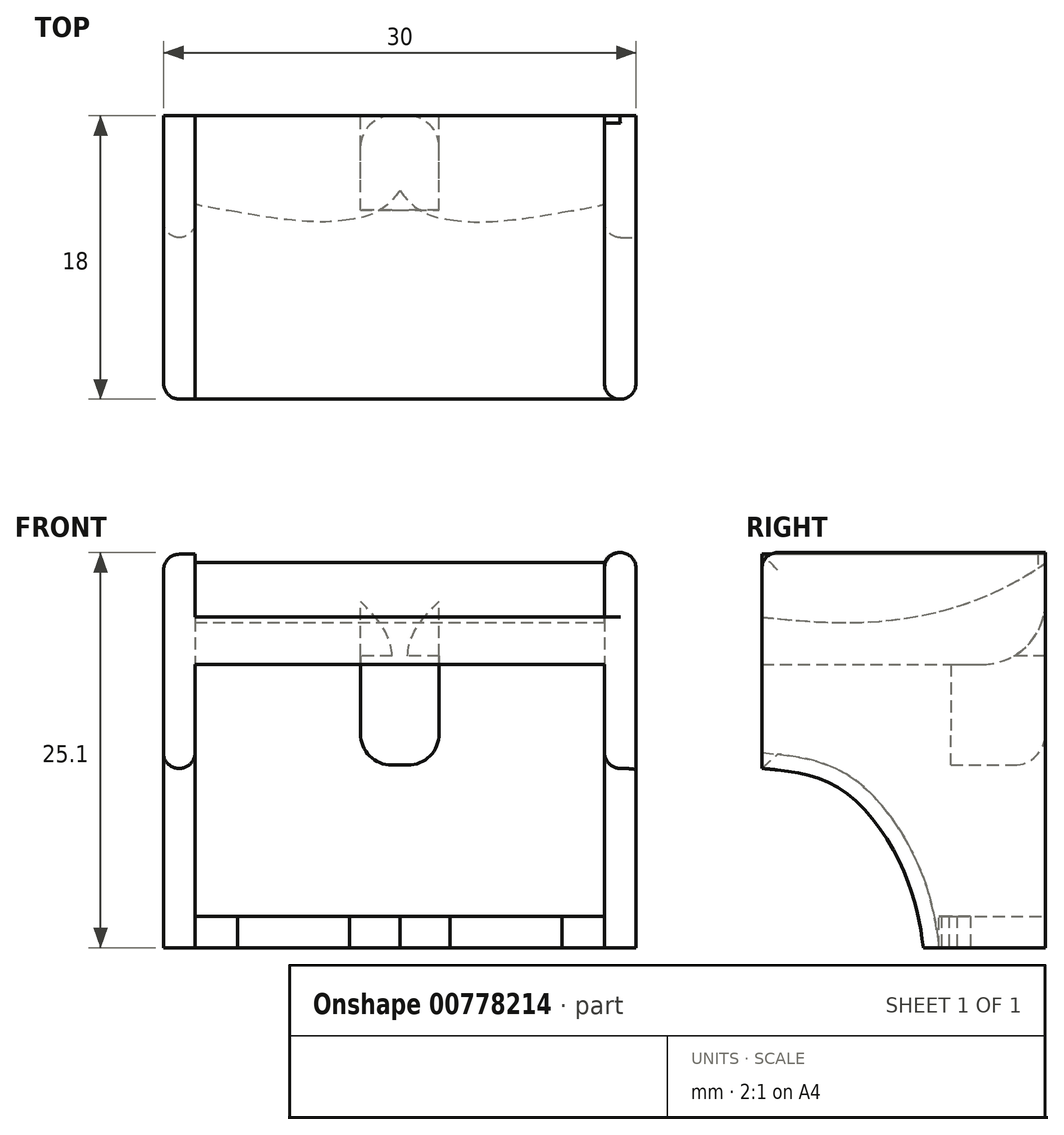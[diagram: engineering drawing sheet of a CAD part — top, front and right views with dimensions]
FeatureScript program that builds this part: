
annotation { "Feature Type Name" : "Feature", "Feature Type Description" : "" }
export const myFeature = defineFeature(function(context is Context, id is Id, definition is map)
    precondition{}
    {
        {
            var Q0;
            Q0=qCreatedBy(makeId("Front.planeOp"),FACE);
            var sketch = newSketch(context, id + "F0", { "sketchPlane" : qUnion([Q0])});
            skLineSegment(sketch, "E0.bottom", {"start": v(0, 0) * mm, "end": v(30, 0) * mm});
            skLineSegment(sketch, "E0.top", {"start": v(0, 20) * mm, "end": v(30, 20) * mm});
            skLineSegment(sketch, "E0.left", {"start": v(0, 0) * mm, "end": v(0, 20) * mm});
            skLineSegment(sketch, "E0.right", {"start": v(30, 0) * mm, "end": v(30, 20) * mm});
            skLineSegment(sketch, "E1.0", {"start": v(2, 18) * mm, "end": v(12.5, 18) * mm});
            skLineSegment(sketch, "E1.1", {"start": v(2, 2) * mm, "end": v(2, 18) * mm});
            skLineSegment(sketch, "E1.2", {"start": v(2, 2) * mm, "end": v(28, 2) * mm});
            skLineSegment(sketch, "E1.3", {"start": v(28, 2) * mm, "end": v(28, 18) * mm});
            skLineSegment(sketch, "E2", {"start": v(15, 11.6) * mm, "end": v(15, 0) * mm, "construction": true});
            skLineSegment(sketch, "E3.bottom", {"start": v(15, 20) * mm, "end": v(17.5, 20) * mm});
            skLineSegment(sketch, "E3.top", {"start": v(15, 11.6) * mm, "end": v(17.5, 11.6) * mm});
            skLineSegment(sketch, "E3.right", {"start": v(17.5, 18) * mm, "end": v(17.5, 11.6) * mm});
            skLineSegment(sketch, "E4.MirrorCS", {"start": v(15, 11.6) * mm, "end": v(12.5, 11.6) * mm});
            skLineSegment(sketch, "E5.MirrorCS", {"start": v(12.5, 18) * mm, "end": v(12.5, 11.6) * mm});
            skLineSegment(sketch, "E6.trimOffspring", {"start": v(17.5, 18) * mm, "end": v(28, 18) * mm});
            skLineSegment(sketch, "E7", {"start": v(12.5, 18) * mm, "end": v(17.5, 18) * mm});
            skPoint(sketch, "E8.orphan", {"position": v(12.5, 20) * mm});
            skSolve(sketch);
        }
        {
            var Q0;
            Q0=makeQuery(id+"F0.imprint","IMPRINT",FACE,{"disambiguationData":[TD([[makeQuery(id+"F0.imprint","IMPRINT",EDGE,{"derivedFrom":sQuery(id+"F0.wireOp",EDGE,"E0.bottom")}),1.0]])]});
            var Q1;
            Q1=makeQuery(id+"F0.imprint","IMPRINT",FACE,{"disambiguationData":[TD([[makeQuery(id+"F0.imprint","IMPRINT",EDGE,{"derivedFrom":sQuery(id+"F0.wireOp",EDGE,"E3.top")}),1.0]])]});
            extrude(context, id + "F1", {"entities" : qUnion([Q0, Q1]), "depth" : 18 * mm, "offsetDistance" : 25 * mm});
        }
        {
            var Q0;
            Q0=makeQuery(id+"F1.opExtrude","SWEPT_FACE",FACE,{"disambiguationData":[OSD([sQuery(id+"F0.wireOp",EDGE,"E0.bottom")])]});
            var sketch = newSketch(context, id + "F2", { "sketchPlane" : qUnion([Q0])});
            skLineSegment(sketch, "E9", {"start": v(2, 18) * mm, "end": v(2, 0) * mm});
            skLineSegment(sketch, "E10", {"start": v(28, 18) * mm, "end": v(28, 0) * mm});
            skLineSegment(sketch, "E11", {"start": v(15, 18) * mm, "end": v(15, 0) * mm, "construction": true});
            skFitSpline(sketch, "E12", {"points": [v(15, 4.76) * mm, v(11.82, 6.58) * mm, v(2, 5.61) * mm, v(2, 5.6) * mm], "startDerivative": vector(-5.14, 6.62) * mm, "endDerivative": vector(0.38, -0.52) * mm});
            skFitSpline(sketch, "E13.MirrorCS", {"points": [v(15, 4.76) * mm, v(18.18, 6.58) * mm, v(28, 5.61) * mm, v(28, 5.6) * mm], "startDerivative": vector(5.14, 6.62) * mm, "endDerivative": vector(-0.38, -0.52) * mm});
            skFitSpline(sketch, "E14", {"points": [v(15, 4.76) * mm, v(11.82, 6.58) * mm, v(2, 5.61) * mm], "startDerivative": vector(-7, 6.03) * mm, "endDerivative": vector(-18.1, -3.55) * mm});
            skFitSpline(sketch, "E15.MirrorCS", {"points": [v(15, 4.76) * mm, v(18.18, 6.58) * mm, v(28, 5.61) * mm], "startDerivative": vector(7, 6.03) * mm, "endDerivative": vector(18.1, -3.55) * mm});
            skSolve(sketch);
        }
        {
            var Q0;
            {var subQ3=sQuery(id+"F2.wireOp",EDGE,"E9");var subQ5=makeQuery(id+"F1.opExtrude","CAP_EDGE",EDGE,{"disambiguationData":[OSD([sQuery(id+"F0.wireOp",EDGE,"E0.bottom")])],"isStart":false});var subQ6=makeQuery(id+"F2.imprint","INTERSECT",VERTEX,{"derivedFrom":[subQ5,subQ3]});Q0=makeQuery(id+"F2.imprint","IMPRINT",FACE,{"disambiguationData":[TD([[makeQuery(id+"F2.imprint","IMPRINT",EDGE,{"disambiguationData":[TD([[subQ6,-1.0]])],"derivedFrom":subQ3}),1.0]])]});}
            extrude(context, id + "F3", {"entities" : qUnion([Q0]), "operationType" : NewBodyOperationType.REMOVE, "oppositeDirection" : true, "depth" : 2 * mm, "offsetDistance" : 25 * mm});
        }
        {
            var Q0;
            Q0=makeQuery(id+"F1.opExtrude","SWEPT_FACE",FACE,{"disambiguationData":[OSD([sQuery(id+"F0.wireOp",EDGE,"E0.right")])]});
            var sketch = newSketch(context, id + "F4", { "sketchPlane" : qUnion([Q0])});
            skPoint(sketch, "E16.1.internal.snap0", {"position": v(-18, 10) * mm});
            skFitSpline(sketch, "E16", {"points": [v(-18, 11.4) * mm, v(-12.88, 10) * mm, v(-8.83, 4.5) * mm, v(-7.74, 0) * mm], "startDerivative": vector(16.41, -1.59) * mm, "endDerivative": vector(2.12, -14.06) * mm});
            skSolve(sketch);
        }
        {
            var Q0;
            {var subQ0=sQuery(id+"F4.wireOp",EDGE,"E16");Q0=makeQuery(id+"F4.imprint","IMPRINT",FACE,{"disambiguationData":[TD([[makeQuery(id+"F4.imprint","IMPRINT",EDGE,{"derivedFrom":subQ0}),-1.0]])]});}
            extrude(context, id + "F5", {"entities" : qUnion([Q0]), "operationType" : NewBodyOperationType.REMOVE, "endBound" : BoundingType.THROUGH_ALL, "oppositeDirection" : true, "depth" : 25 * mm, "offsetDistance" : 25 * mm});
        }
        {
            var Q0;
            Q0=makeQuery(id+"F1.opExtrude","SWEPT_FACE",FACE,{"disambiguationData":[OSD([sQuery(id+"F0.wireOp",EDGE,"E0.top"),sQuery(id+"F0.wireOp",EDGE,"E3.bottom")])]});
            extrude(context, id + "F6", {"entities" : qUnion([Q0]), "operationType" : NewBodyOperationType.ADD, "depth" : 5 * mm, "offsetDistance" : 25 * mm});
        }
        {
            var Q0;
            {var subQ0=sQuery(id+"F0.wireOp",EDGE,"E0.right");Q0=makeQuery(id+"F6.boolean.opBoolean","MERGE",FACE,{"derivedFrom":[makeQuery(id+"F1.opExtrude","SWEPT_FACE",FACE,{"disambiguationData":[OSD([subQ0])]}),makeQuery(id+"F6.opExtrude","SWEPT_FACE",FACE,{"disambiguationData":[OSD([sQuery(id+"F0.wireOp",EDGE,"E0.top"),subQ0])]})]});}
            var sketch = newSketch(context, id + "F7", { "sketchPlane" : qUnion([Q0])});
            skLineSegment(sketch, "E17", {"start": v(-18, 20.2) * mm, "end": v(0, 20.2) * mm, "construction": true});
            skFitSpline(sketch, "E18", {"points": [v(-18, 21) * mm, v(-11.59, 20.68) * mm, v(-3.7, 22.37) * mm, v(0, 24.47) * mm, v(0, 24.5) * mm], "startDerivative": vector(18.68, -1.89) * mm, "endDerivative": vector(-0.52, 1.05) * mm});
            skSolve(sketch);
        }
        {
            var Q0;
            {var subQ0=sQuery(id+"F0.wireOp",EDGE,"E3.bottom");var subQ1=sQuery(id+"F0.wireOp",EDGE,"E0.top");Q0=makeQuery(id+"F6.boolean.opBoolean","MERGE",FACE,{"derivedFrom":[makeQuery(id+"F1.opExtrude","CAP_FACE",FACE,{"disambiguationData":[OSD([sQuery(id+"F0.wireOp",EDGE,"E0.bottom"),subQ1,sQuery(id+"F0.wireOp",EDGE,"E0.left"),sQuery(id+"F0.wireOp",EDGE,"E0.right"),sQuery(id+"F0.wireOp",EDGE,"E1.0"),sQuery(id+"F0.wireOp",EDGE,"E1.1"),sQuery(id+"F0.wireOp",EDGE,"E1.2"),sQuery(id+"F0.wireOp",EDGE,"E1.3"),subQ0,sQuery(id+"F0.wireOp",EDGE,"E3.top"),sQuery(id+"F0.wireOp",EDGE,"E3.right"),sQuery(id+"F0.wireOp",EDGE,"E4.MirrorCS"),sQuery(id+"F0.wireOp",EDGE,"E5.MirrorCS"),sQuery(id+"F0.wireOp",EDGE,"E6.trimOffspring")])],"isStart":false}),makeQuery(id+"F6.opExtrude","SWEPT_FACE",FACE,{"disambiguationData":[OSD([subQ1,subQ0]),TDD([makeQuery(id+"F1.opExtrude","CAP_EDGE",EDGE,{"disambiguationData":[OSD([subQ1,subQ0])],"isStart":false})])]})]});}
            var sketch = newSketch(context, id + "F8", { "sketchPlane" : qUnion([Q0])});
            skLineSegment(sketch, "E19", {"start": v(2, 18) * mm, "end": v(2, 25) * mm, "construction": true});
            skSolve(sketch);
        }
        {
            var Q0;
            {var subQ1=sQuery(id+"F0.wireOp",EDGE,"E0.right");var subQ2=sQuery(id+"F0.wireOp",EDGE,"E0.top");var subQ6=makeQuery(id+"F6.opExtrude","CAP_EDGE",EDGE,{"disambiguationData":[OSD([subQ2,subQ1])],"isStart":false});Q0=makeQuery(id+"F7.imprint","IMPRINT",FACE,{"disambiguationData":[TD([[makeQuery(id+"F7.imprint","IMPRINT",EDGE,{"derivedFrom":subQ6}),-1.0]])]});}
            extrude(context, id + "F9", {"entities" : qUnion([Q0]), "operationType" : NewBodyOperationType.REMOVE, "oppositeDirection" : true, "depth" : 28 * mm, "offsetDistance" : 25 * mm});
        }
        {
            var Q0;
            {var subQ0=sQuery(id+"F0.wireOp",EDGE,"E0.right");Q0=makeQuery(id+"F6.boolean.opBoolean","MERGE",FACE,{"derivedFrom":[makeQuery(id+"F1.opExtrude","SWEPT_FACE",FACE,{"disambiguationData":[OSD([subQ0])]}),makeQuery(id+"F6.opExtrude","SWEPT_FACE",FACE,{"disambiguationData":[OSD([sQuery(id+"F0.wireOp",EDGE,"E0.top"),subQ0])]})]});}
            var sketch = newSketch(context, id + "F10", { "sketchPlane" : qUnion([Q0])});
            skLineSegment(sketch, "E20", {"start": v(-18, 20.1) * mm, "end": v(0, 20.1) * mm, "construction": true});
            skFitSpline(sketch, "E21", {"points": [v(-18, 20.91) * mm, v(-11.59, 20.59) * mm, v(-3.7, 22.28) * mm, v(0, 24.38) * mm, v(0, 24.42) * mm], "startDerivative": vector(18.68, -1.89) * mm, "endDerivative": vector(-0.52, 1.05) * mm});
            skLineSegment(sketch, "E22", {"start": v(-18, 20.1) * mm, "end": v(0, 20.1) * mm});
            skSolve(sketch);
        }
        {
            var Q0;
            {var subQ7=sQuery(id+"F10.wireOp",EDGE,"E22");Q0=makeQuery(id+"F10.imprint","IMPRINT",FACE,{"disambiguationData":[TD([[makeQuery(id+"F10.imprint","IMPRINT",EDGE,{"derivedFrom":subQ7}),1.0]])]});}
            extrude(context, id + "F11", {"entities" : qUnion([Q0]), "operationType" : NewBodyOperationType.REMOVE, "oppositeDirection" : true, "depth" : 2 * mm, "offsetDistance" : 25 * mm});
        }
        {
            var Q0;
            Q0=makeQuery(id+"F11.boolean.opBoolean","COPY",FACE,{"derivedFrom":makeQuery(id+"F11.opExtrude","SWEPT_FACE",FACE,{"disambiguationData":[OSD([sQuery(id+"F10.wireOp",EDGE,"E22")])]})});
            extrude(context, id + "F12", {"entities" : qUnion([Q0]), "operationType" : NewBodyOperationType.ADD, "depth" : 5 * mm, "offsetDistance" : 25 * mm});
        }
        {
            var Q0;
            Q0=makeQuery(id+"F1.opExtrude","CAP_EDGE",EDGE,{"disambiguationData":[OSD([sQuery(id+"F0.wireOp",EDGE,"E6.trimOffspring")])],"isStart":true});
            var Q1;
            Q1=makeQuery(id+"F1.opExtrude","CAP_EDGE",EDGE,{"disambiguationData":[OSD([sQuery(id+"F0.wireOp",EDGE,"E1.0")])],"isStart":true});
            fillet(context, id + "F13", {"entities" : qUnion([Q0, Q1]), "radius" : 4 * mm, "tangentPropagation" : true, "allowEdgeOverflow" : false});
        }
        {
            var Q0;
            Q0=makeQuery(id+"F1.opExtrude","CAP_EDGE",EDGE,{"disambiguationData":[OSD([sQuery(id+"F0.wireOp",EDGE,"E3.right")])],"isStart":true});
            var Q1;
            Q1=makeQuery(id+"F1.opExtrude","CAP_EDGE",EDGE,{"disambiguationData":[OSD([sQuery(id+"F0.wireOp",EDGE,"E5.MirrorCS")])],"isStart":true});
            fillet(context, id + "F14", {"entities" : qUnion([Q0, Q1]), "radius" : 2 * mm, "tangentPropagation" : true, "allowEdgeOverflow" : false});
        }
        {
            var Q0;
            {var subQ11=sQuery(id+"F0.wireOp",EDGE,"E1.0");Q0=makeQuery(id+"F8.imprint","IMPRINT",FACE,{"disambiguationData":[TD([[makeQuery(id+"F8.imprint","IMPRINT",EDGE,{"derivedFrom":makeQuery(id+"F1.opExtrude","CAP_EDGE",EDGE,{"disambiguationData":[OSD([subQ11])],"isStart":false})}),1.0]])]});}
            var sketch = newSketch(context, id + "F15", { "sketchPlane" : qUnion([Q0])});
            skLineSegment(sketch, "E23", {"start": v(17.5, 18) * mm, "end": v(12.5, 18) * mm});
            skSolve(sketch);
        }
        {
            var Q0;
            Q0=makeQuery(id+"F1.opExtrude","SWEPT_FACE",FACE,{"disambiguationData":[OSD([sQuery(id+"F0.wireOp",EDGE,"E3.top"),sQuery(id+"F0.wireOp",EDGE,"E4.MirrorCS")])]});
            var sketch = newSketch(context, id + "F16", { "sketchPlane" : qUnion([Q0])});
            skLineSegment(sketch, "E24", {"start": v(12.5, 12) * mm, "end": v(17.5, 12) * mm});
            skSolve(sketch);
        }
        {
            var Q0;
            {var subQ0=sQuery(id+"F16.wireOp",EDGE,"E24");Q0=makeQuery(id+"F16.imprint","IMPRINT",FACE,{"disambiguationData":[TD([[makeQuery(id+"F16.imprint","IMPRINT",EDGE,{"derivedFrom":subQ0}),1.0]])]});}
            extrude(context, id + "F17", {"entities" : qUnion([Q0]), "operationType" : NewBodyOperationType.REMOVE, "oppositeDirection" : true, "depth" : 6.4 * mm, "offsetDistance" : 25 * mm});
        }
        {
            var Q0;
            {var subQ0=sQuery(id+"F7.wireOp",EDGE,"E18");var subQ1=sQuery(id+"F0.wireOp",EDGE,"E0.right");var subQ2=sQuery(id+"F0.wireOp",EDGE,"E0.top");Q0=makeQuery(id+"F9.boolean.opBoolean","COPY",EDGE,{"derivedFrom":makeQuery(id+"F9.opExtrude","SWEPT_EDGE",EDGE,{"disambiguationData":[OSD([subQ2,subQ1,subQ0]),TDD([makeQuery(id+"F7.imprint","INTERSECT",VERTEX,{"derivedFrom":[makeQuery(id+"F6.boolean.opBoolean","MERGE",EDGE,{"derivedFrom":[makeQuery(id+"F1.opExtrude","CAP_EDGE",EDGE,{"disambiguationData":[OSD([subQ1])],"isStart":false}),makeQuery(id+"F6.opExtrude","SWEPT_EDGE",EDGE,{"disambiguationData":[OSD([subQ2,subQ1]),TDD([makeQuery(id+"F1.opExtrude","CAP_VERTEX",VERTEX,{"disambiguationData":[OSD([subQ2,subQ1])],"isStart":false})])]})]}),subQ0]})])]})});}
            var Q1;
            Q1=makeQuery(id+"F17.boolean.opBoolean","MERGE",EDGE,{"derivedFrom":[makeQuery(id+"F1.opExtrude","CAP_EDGE",EDGE,{"disambiguationData":[OSD([sQuery(id+"F0.wireOp",EDGE,"E1.0")])],"isStart":false}),makeQuery(id+"F1.opExtrude","CAP_EDGE",EDGE,{"disambiguationData":[OSD([sQuery(id+"F0.wireOp",EDGE,"E6.trimOffspring")])],"isStart":false}),makeQuery(id+"F17.opExtrude","CAP_EDGE",EDGE,{"disambiguationData":[OSD([sQuery(id+"F0.wireOp",EDGE,"E3.top"),sQuery(id+"F0.wireOp",EDGE,"E4.MirrorCS")])],"isStart":false})]});
            var Q2;
            Q2=makeQuery(id+"F3.boolean.opBoolean","MERGE",EDGE,{"derivedFrom":[makeQuery(id+"F1.opExtrude","CAP_EDGE",EDGE,{"disambiguationData":[OSD([sQuery(id+"F0.wireOp",EDGE,"E1.3")])],"isStart":false}),makeQuery(id+"F3.opExtrude","SWEPT_EDGE",EDGE,{"disambiguationData":[OSD([sQuery(id+"F0.wireOp",EDGE,"E0.bottom"),sQuery(id+"F2.wireOp",EDGE,"E10")])]})]});
            var Q3;
            {var subQ0=sQuery(id+"F10.wireOp",EDGE,"E22");var subQ1=sQuery(id+"F0.wireOp",EDGE,"E0.right");var subQ2=sQuery(id+"F0.wireOp",EDGE,"E0.top");var subQ3=makeQuery(id+"F6.boolean.opBoolean","MERGE",EDGE,{"derivedFrom":[makeQuery(id+"F1.opExtrude","CAP_EDGE",EDGE,{"disambiguationData":[OSD([subQ1])],"isStart":false}),makeQuery(id+"F6.opExtrude","SWEPT_EDGE",EDGE,{"disambiguationData":[OSD([subQ2,subQ1]),TDD([makeQuery(id+"F1.opExtrude","CAP_VERTEX",VERTEX,{"disambiguationData":[OSD([subQ2,subQ1])],"isStart":false})])]})]});Q3=makeQuery(id+"F12.boolean.opBoolean","MERGE",EDGE,{"derivedFrom":[makeQuery(id+"F11.boolean.opBoolean","SPLIT",EDGE,{"disambiguationData":[TD([makeQuery(id+"F11.opExtrude","SWEPT_FACE",FACE,{"disambiguationData":[OSD([subQ0])]})])],"derivedFrom":subQ3}),makeQuery(id+"F11.boolean.opBoolean","SPLIT",EDGE,{"disambiguationData":[TD([makeQuery(id+"F9.boolean.opBoolean","COPY",FACE,{"derivedFrom":makeQuery(id+"F9.opExtrude","SWEPT_FACE",FACE,{"disambiguationData":[OSD([sQuery(id+"F7.wireOp",EDGE,"E18")])]})})])],"derivedFrom":subQ3}),makeQuery(id+"F12.opExtrude","SWEPT_EDGE",EDGE,{"disambiguationData":[OSD([subQ2,subQ1,subQ0]),TDD([makeQuery(id+"F11.boolean.opBoolean","COPY",VERTEX,{"derivedFrom":makeQuery(id+"F11.opExtrude","CAP_VERTEX",VERTEX,{"disambiguationData":[OSD([subQ2,subQ1,subQ0]),TDD([makeQuery(id+"F10.imprint","INTERSECT",VERTEX,{"derivedFrom":[subQ3,subQ0]})])],"isStart":true})})])]})]});}
            var Q4;
            {var subQ0=sQuery(id+"F10.wireOp",EDGE,"E22");var subQ1=sQuery(id+"F0.wireOp",EDGE,"E0.right");var subQ2=sQuery(id+"F0.wireOp",EDGE,"E0.top");Q4=makeQuery(id+"F12.opExtrude","SWEPT_EDGE",EDGE,{"disambiguationData":[OSD([subQ2,subQ1,subQ0]),TDD([makeQuery(id+"F11.boolean.opBoolean","COPY",VERTEX,{"derivedFrom":makeQuery(id+"F11.opExtrude","CAP_VERTEX",VERTEX,{"disambiguationData":[OSD([subQ2,subQ1,subQ0]),TDD([makeQuery(id+"F10.imprint","INTERSECT",VERTEX,{"derivedFrom":[makeQuery(id+"F6.boolean.opBoolean","MERGE",EDGE,{"derivedFrom":[makeQuery(id+"F1.opExtrude","CAP_EDGE",EDGE,{"disambiguationData":[OSD([subQ1])],"isStart":false}),makeQuery(id+"F6.opExtrude","SWEPT_EDGE",EDGE,{"disambiguationData":[OSD([subQ2,subQ1]),TDD([makeQuery(id+"F1.opExtrude","CAP_VERTEX",VERTEX,{"disambiguationData":[OSD([subQ2,subQ1])],"isStart":false})])]})]}),subQ0]})])],"isStart":false})})])]});}
            var Q5;
            {var subQ0=sQuery(id+"F0.wireOp",EDGE,"E0.left");var subQ1=sQuery(id+"F0.wireOp",EDGE,"E0.top");Q5=makeQuery(id+"F6.boolean.opBoolean","MERGE",EDGE,{"derivedFrom":[makeQuery(id+"F1.opExtrude","CAP_EDGE",EDGE,{"disambiguationData":[OSD([subQ0])],"isStart":false}),makeQuery(id+"F6.opExtrude","SWEPT_EDGE",EDGE,{"disambiguationData":[OSD([subQ1,subQ0]),TDD([makeQuery(id+"F1.opExtrude","CAP_VERTEX",VERTEX,{"disambiguationData":[OSD([subQ1,subQ0])],"isStart":false})])]})]});}
            var Q6;
            Q6=makeQuery(id+"F3.boolean.opBoolean","MERGE",EDGE,{"derivedFrom":[makeQuery(id+"F1.opExtrude","CAP_EDGE",EDGE,{"disambiguationData":[OSD([sQuery(id+"F0.wireOp",EDGE,"E1.1")])],"isStart":false}),makeQuery(id+"F3.opExtrude","SWEPT_EDGE",EDGE,{"disambiguationData":[OSD([sQuery(id+"F0.wireOp",EDGE,"E0.bottom"),sQuery(id+"F2.wireOp",EDGE,"E9")])]})]});
            var Q7;
            Q7=makeQuery(id+"F5.boolean.opBoolean","INTERSECT",EDGE,{"derivedFrom":[makeQuery(id+"F3.boolean.opBoolean","MERGE",FACE,{"derivedFrom":[makeQuery(id+"F1.opExtrude","SWEPT_FACE",FACE,{"disambiguationData":[OSD([sQuery(id+"F0.wireOp",EDGE,"E1.1")])]}),makeQuery(id+"F3.opExtrude","SWEPT_FACE",FACE,{"disambiguationData":[OSD([sQuery(id+"F2.wireOp",EDGE,"E9")])]})]}),makeQuery(id+"F5.opExtrude","SWEPT_FACE",FACE,{"disambiguationData":[OSD([sQuery(id+"F4.wireOp",EDGE,"E16")])]})]});
            var Q8;
            Q8=makeQuery(id+"F5.boolean.opBoolean","INTERSECT",EDGE,{"derivedFrom":[makeQuery(id+"F1.opExtrude","SWEPT_FACE",FACE,{"disambiguationData":[OSD([sQuery(id+"F0.wireOp",EDGE,"E0.left")])]}),makeQuery(id+"F5.opExtrude","SWEPT_FACE",FACE,{"disambiguationData":[OSD([sQuery(id+"F4.wireOp",EDGE,"E16")])]})]});
            var Q9;
            Q9=makeQuery(id+"F5.boolean.opBoolean","INTERSECT",EDGE,{"derivedFrom":[makeQuery(id+"F3.boolean.opBoolean","MERGE",FACE,{"derivedFrom":[makeQuery(id+"F1.opExtrude","SWEPT_FACE",FACE,{"disambiguationData":[OSD([sQuery(id+"F0.wireOp",EDGE,"E1.3")])]}),makeQuery(id+"F3.opExtrude","SWEPT_FACE",FACE,{"disambiguationData":[OSD([sQuery(id+"F2.wireOp",EDGE,"E10")])]})]}),makeQuery(id+"F5.opExtrude","SWEPT_FACE",FACE,{"disambiguationData":[OSD([sQuery(id+"F4.wireOp",EDGE,"E16")])]})]});
            var Q10;
            Q10=makeQuery(id+"F5.boolean.opBoolean","COPY",EDGE,{"derivedFrom":makeQuery(id+"F5.opExtrude","CAP_EDGE",EDGE,{"disambiguationData":[OSD([sQuery(id+"F4.wireOp",EDGE,"E16")])],"isStart":true})});
            var Q11;
            Q11=makeQuery(id+"F3.boolean.opBoolean","COPY",EDGE,{"derivedFrom":makeQuery(id+"F3.opExtrude","CAP_EDGE",EDGE,{"disambiguationData":[OSD([sQuery(id+"F2.wireOp",EDGE,"E15.MirrorCS")])],"isStart":false})});
            var Q12;
            Q12=makeQuery(id+"F3.boolean.opBoolean","COPY",EDGE,{"derivedFrom":makeQuery(id+"F3.opExtrude","CAP_EDGE",EDGE,{"disambiguationData":[OSD([sQuery(id+"F2.wireOp",EDGE,"E15.MirrorCS")])],"isStart":true})});
            var Q13;
            Q13=makeQuery(id+"F3.boolean.opBoolean","COPY",EDGE,{"derivedFrom":makeQuery(id+"F3.opExtrude","CAP_EDGE",EDGE,{"disambiguationData":[OSD([sQuery(id+"F2.wireOp",EDGE,"E14")])],"isStart":false})});
            var Q14;
            Q14=makeQuery(id+"F3.boolean.opBoolean","COPY",EDGE,{"derivedFrom":makeQuery(id+"F3.opExtrude","CAP_EDGE",EDGE,{"disambiguationData":[OSD([sQuery(id+"F2.wireOp",EDGE,"E14")])],"isStart":true})});
            var Q15;
            {var subQ0=sQuery(id+"F10.wireOp",EDGE,"E22");Q15=makeQuery(id+"F12.opExtrude","CAP_EDGE",EDGE,{"disambiguationData":[OSD([subQ0]),TDD([makeQuery(id+"F11.boolean.opBoolean","COPY",EDGE,{"derivedFrom":makeQuery(id+"F11.opExtrude","CAP_EDGE",EDGE,{"disambiguationData":[OSD([subQ0])],"isStart":false})})])],"isStart":false});}
            var Q16;
            {var subQ0=sQuery(id+"F10.wireOp",EDGE,"E22");Q16=makeQuery(id+"F12.opExtrude","CAP_EDGE",EDGE,{"disambiguationData":[OSD([subQ0]),TDD([makeQuery(id+"F11.boolean.opBoolean","COPY",EDGE,{"derivedFrom":makeQuery(id+"F11.opExtrude","CAP_EDGE",EDGE,{"disambiguationData":[OSD([subQ0])],"isStart":true})})])],"isStart":false});}
            var Q17;
            {var subQ0=sQuery(id+"F0.wireOp",EDGE,"E0.right");var subQ1=sQuery(id+"F0.wireOp",EDGE,"E0.top");Q17=makeQuery(id+"F9.boolean.opBoolean","COPY",EDGE,{"derivedFrom":makeQuery(id+"F9.opExtrude","CAP_EDGE",EDGE,{"disambiguationData":[OSD([subQ1,subQ0]),TDD([makeQuery(id+"F7.imprint","IMPRINT",EDGE,{"derivedFrom":makeQuery(id+"F6.opExtrude","CAP_EDGE",EDGE,{"disambiguationData":[OSD([subQ1,subQ0])],"isStart":false})})])],"isStart":false})});}
            var Q18;
            Q18=makeQuery(id+"F6.opExtrude","CAP_EDGE",EDGE,{"disambiguationData":[OSD([sQuery(id+"F0.wireOp",EDGE,"E0.top"),sQuery(id+"F0.wireOp",EDGE,"E0.left")])],"isStart":false});
            fillet(context, id + "F18", {"entities" : qUnion([Q0, Q1, Q2, Q3, Q4, Q5, Q6, Q7, Q8, Q9, Q10, Q11, Q12, Q13, Q14, Q15, Q16, Q17, Q18]), "radius" : 1 * mm, "tangentPropagation" : true, "allowEdgeOverflow" : false});
        }
        {
            var Q0;
            Q0=makeQuery(id+"F1.opExtrude","SWEPT_EDGE",EDGE,{"disambiguationData":[OSD([sQuery(id+"F0.wireOp",EDGE,"E4.MirrorCS"),sQuery(id+"F0.wireOp",EDGE,"E5.MirrorCS")])]});
            var Q1;
            Q1=makeQuery(id+"F1.opExtrude","SWEPT_EDGE",EDGE,{"disambiguationData":[OSD([sQuery(id+"F0.wireOp",EDGE,"E3.top"),sQuery(id+"F0.wireOp",EDGE,"E3.right")])]});
            fillet(context, id + "F19", {"entities" : qUnion([Q0, Q1]), "radius" : 2 * mm, "tangentPropagation" : true, "allowEdgeOverflow" : false});
        }
        {
            var Q0;
            Q0=makeQuery(id+"F17.boolean.opBoolean","COPY",FACE,{"derivedFrom":makeQuery(id+"F17.opExtrude","SWEPT_FACE",FACE,{"disambiguationData":[OSD([sQuery(id+"F16.wireOp",EDGE,"E24")])]})});
            extrude(context, id + "F20", {"entities" : qUnion([Q0]), "operationType" : NewBodyOperationType.REMOVE, "oppositeDirection" : true, "depth" : 6 * mm, "offsetDistance" : 25 * mm});
        }
        {
            var Q0;
            {var subQ0=sQuery(id+"F0.wireOp",EDGE,"E0.right");var subQ1=sQuery(id+"F0.wireOp",EDGE,"E0.top");var subQ2=makeQuery(id+"F6.boolean.opBoolean","MERGE",EDGE,{"derivedFrom":[makeQuery(id+"F1.opExtrude","CAP_EDGE",EDGE,{"disambiguationData":[OSD([subQ0])],"isStart":false}),makeQuery(id+"F6.opExtrude","SWEPT_EDGE",EDGE,{"disambiguationData":[OSD([subQ1,subQ0]),TDD([makeQuery(id+"F1.opExtrude","CAP_VERTEX",VERTEX,{"disambiguationData":[OSD([subQ1,subQ0])],"isStart":false})])]})]});Q0=makeQuery(id+"F9.boolean.opBoolean","COPY",EDGE,{"derivedFrom":makeQuery(id+"F9.opExtrude","CAP_EDGE",EDGE,{"disambiguationData":[OSD([subQ1,subQ0]),TDD([makeQuery(id+"F7.imprint","IMPRINT",EDGE,{"disambiguationData":[TD([[makeQuery(id+"F7.imprint","INTERSECT",VERTEX,{"derivedFrom":[subQ2,sQuery(id+"F7.wireOp",EDGE,"E18")]}),-1.0]])],"derivedFrom":subQ2})])],"isStart":false})});}
            var Q1;
            {var subQ0=sQuery(id+"F10.wireOp",EDGE,"E22");var subQ1=sQuery(id+"F0.wireOp",EDGE,"E0.right");var subQ2=sQuery(id+"F0.wireOp",EDGE,"E0.top");Q1=makeQuery(id+"F18.opFillet","BLEND_EDGE",EDGE,{"blendedFrom":[makeQuery(id+"F12.opExtrude","CAP_EDGE",EDGE,{"disambiguationData":[OSD([subQ0]),TDD([makeQuery(id+"F11.boolean.opBoolean","COPY",EDGE,{"derivedFrom":makeQuery(id+"F11.opExtrude","CAP_EDGE",EDGE,{"disambiguationData":[OSD([subQ0])],"isStart":false})})])],"isStart":false}),makeQuery(id+"F12.opExtrude","SWEPT_EDGE",EDGE,{"disambiguationData":[OSD([subQ2,subQ1,subQ0]),TDD([makeQuery(id+"F11.boolean.opBoolean","COPY",VERTEX,{"derivedFrom":makeQuery(id+"F11.opExtrude","CAP_VERTEX",VERTEX,{"disambiguationData":[OSD([subQ2,subQ1,subQ0]),TDD([makeQuery(id+"F10.imprint","INTERSECT",VERTEX,{"derivedFrom":[makeQuery(id+"F6.boolean.opBoolean","MERGE",EDGE,{"derivedFrom":[makeQuery(id+"F1.opExtrude","CAP_EDGE",EDGE,{"disambiguationData":[OSD([subQ1])],"isStart":false}),makeQuery(id+"F6.opExtrude","SWEPT_EDGE",EDGE,{"disambiguationData":[OSD([subQ2,subQ1]),TDD([makeQuery(id+"F1.opExtrude","CAP_VERTEX",VERTEX,{"disambiguationData":[OSD([subQ2,subQ1])],"isStart":false})])]})]}),subQ0]})])],"isStart":false})})])]})],"blendedInto":[]});}
            fillet(context, id + "F21", {"entities" : qUnion([Q0, Q1]), "radius" : 1 * mm, "tangentPropagation" : true, "allowEdgeOverflow" : false});
        }
    });
